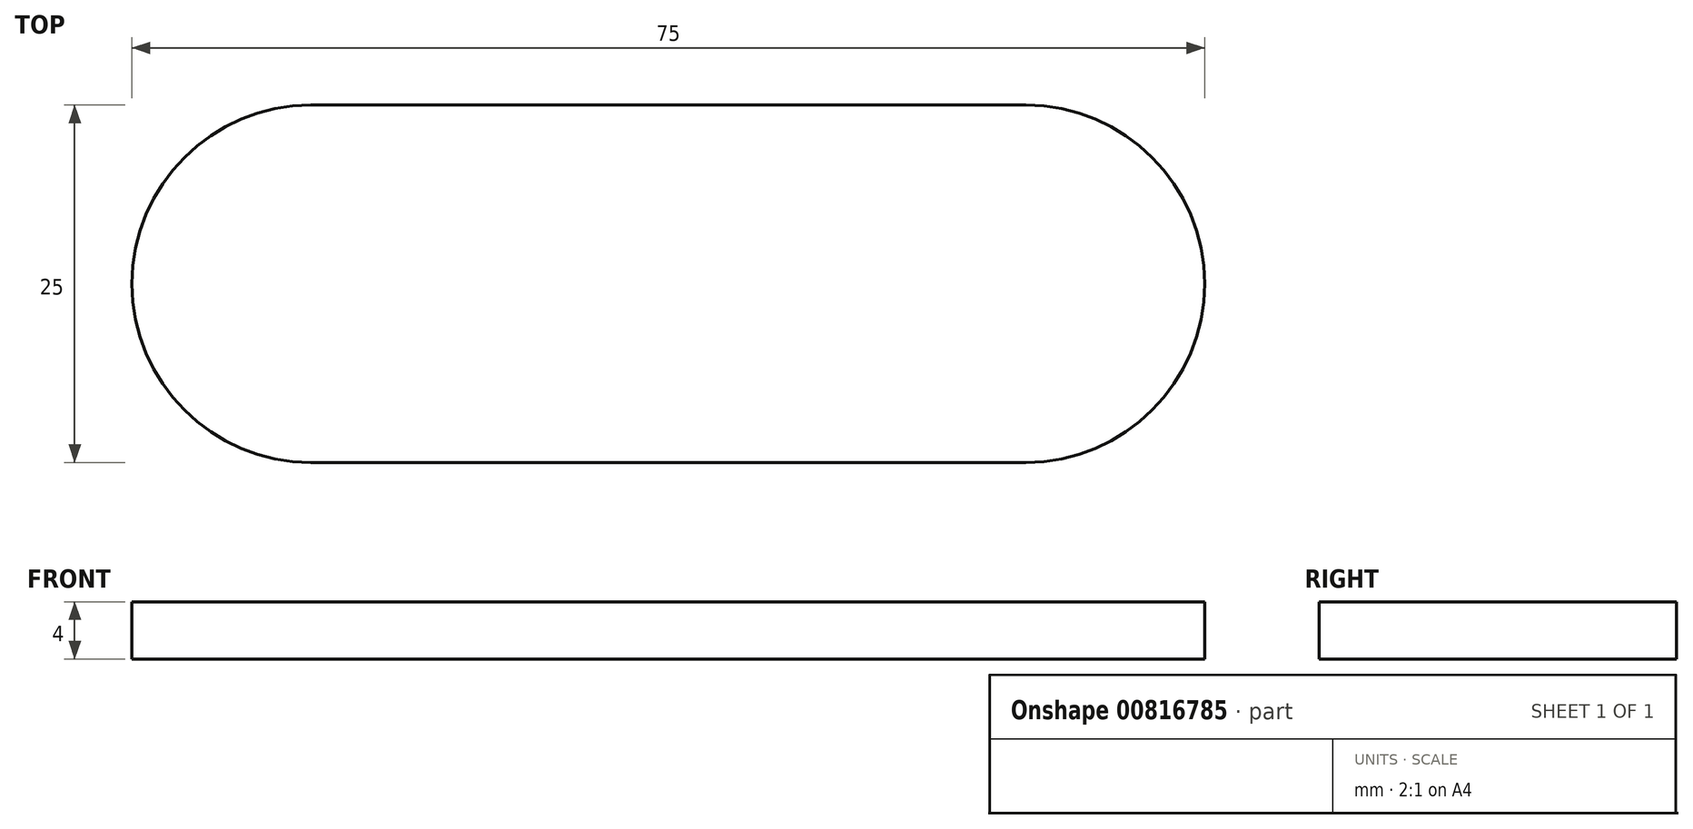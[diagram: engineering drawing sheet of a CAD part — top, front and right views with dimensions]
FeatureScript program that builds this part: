
annotation { "Feature Type Name" : "Feature", "Feature Type Description" : "" }
export const myFeature = defineFeature(function(context is Context, id is Id, definition is map)
    precondition{}
    {
        {
            var Q0;
            Q0=qCreatedBy(makeId("Top.planeOp"),FACE);
            var sketch = newSketch(context, id + "F0", { "sketchPlane" : qUnion([Q0])});
            skLineSegment(sketch, "E0.bottom", {"start": v(12.5, 0) * mm, "end": v(62.5, 0) * mm});
            skLineSegment(sketch, "E0.top", {"start": v(12.5, 25) * mm, "end": v(62.5, 25) * mm});
            skArc(sketch, "E1", {"start": v(12.5, 25) * mm, "mid": v(0, 12.5) * mm, "end": v(12.5, 0) * mm});
            skPoint(sketch, "E1.centerSnap0", {"position": v(0, 12.5) * mm});
            skArc(sketch, "E2", {"start": v(62.5, 0) * mm, "mid": v(75, 12.5) * mm, "end": v(62.5, 25) * mm});
            skPoint(sketch, "E2.centerSnap0", {"position": v(75, 12.5) * mm});
            skPoint(sketch, "E0.left.start.orphan", {"position": v(0, 0) * mm});
            skPoint(sketch, "E3.orphan", {"position": v(0, 25) * mm});
            skPoint(sketch, "E4.orphan", {"position": v(75, 25) * mm});
            skPoint(sketch, "E5.orphan", {"position": v(75, 0) * mm});
            skSolve(sketch);
        }
        {
            var Q0;
            Q0 = qSketchRegion(id + "F0", true);
            extrude(context, id + "F1", {"entities" : qUnion([Q0]), "depth" : 4 * mm, "offsetDistance" : 25 * mm});
        }
    });
